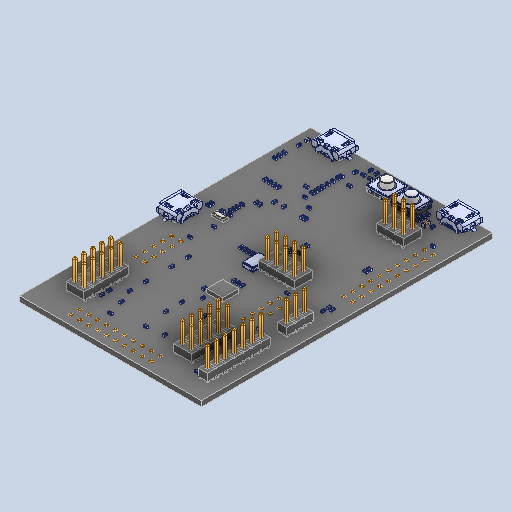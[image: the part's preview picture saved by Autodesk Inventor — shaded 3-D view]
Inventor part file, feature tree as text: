
AUTODESK INVENTOR PART (.ipt)
format: ipt  version: 2024.2 (Build 282272000, 272)  size: 4,771,328 bytes
history: native  units: mm
features: sketch x350, other x149, chamfer x6
ambient origin geometry x8: Origin, YZ Plane, XZ Plane, XY Plane, X Axis, Y Axis, Z Axis, Center Point
bodies: Solid1 (feature_tree), Solid2 (feature_tree), Solid3 (feature_tree), Solid4 (feature_tree), Solid5 (feature_tree), Solid6 (feature_tree), Solid7 (feature_tree), Solid8 (feature_tree), Solid9 (feature_tree), Solid10 (feature_tree), Solid11 (feature_tree), Solid12 (feature_tree), Solid13 (feature_tree), Solid14 (feature_tree), Solid15 (feature_tree), Solid16 (feature_tree), Solid17 (feature_tree), Solid18 (feature_tree), Solid19 (feature_tree), Solid20 (feature_tree), Solid21 (feature_tree), Solid22 (feature_tree), Solid23 (feature_tree), Solid24 (feature_tree), Solid25 (feature_tree), Solid26 (feature_tree), Solid27 (feature_tree), Solid28 (feature_tree), Solid29 (feature_tree), Solid30 (feature_tree), Solid31 (feature_tree), Solid32 (feature_tree), Solid33 (feature_tree), Solid34 (feature_tree), Solid35 (feature_tree), Solid36 (feature_tree), Solid37 (feature_tree), Solid38 (feature_tree), Solid39 (feature_tree), Solid40 (feature_tree), Solid41 (feature_tree), Solid42 (feature_tree), Solid43 (feature_tree), Solid44 (feature_tree), Solid45 (feature_tree), Solid46 (feature_tree), Solid47 (feature_tree), Solid48 (feature_tree), Solid49 (feature_tree), Solid50 (feature_tree), Solid51 (feature_tree), Solid52 (feature_tree), Solid53 (feature_tree), Solid54 (feature_tree), Solid55 (feature_tree), Solid56 (feature_tree), Solid57 (feature_tree), Solid58 (feature_tree), Solid59 (feature_tree), Solid60 (feature_tree), Solid61 (feature_tree), Solid62 (feature_tree), Solid63 (feature_tree), Solid64 (feature_tree), Solid65 (feature_tree), Solid66 (feature_tree), Solid67 (feature_tree), Solid68 (feature_tree), Solid69 (feature_tree), Solid70 (feature_tree), Solid71 (feature_tree), Solid72 (feature_tree), Solid73 (feature_tree), Solid74 (feature_tree), Solid75 (feature_tree), Solid76 (feature_tree), Solid77 (feature_tree), Solid78 (feature_tree), Solid79 (feature_tree), Solid80 (feature_tree), Solid81 (feature_tree), Solid82 (feature_tree), Solid83 (feature_tree), Solid84 (feature_tree), Solid85 (feature_tree), Solid86 (feature_tree), Solid87 (feature_tree), Solid88 (feature_tree), Solid89 (feature_tree), Solid90 (feature_tree), Solid91 (feature_tree), Solid92 (feature_tree), Solid93 (feature_tree), Solid94 (feature_tree), Solid95 (feature_tree), Solid96 (feature_tree), Solid97 (feature_tree), Solid98 (feature_tree), Solid99 (feature_tree), Solid100 (feature_tree), Solid101 (feature_tree), Solid102 (feature_tree), Solid103 (feature_tree), Solid104 (feature_tree), Solid105 (feature_tree), Solid106 (feature_tree), Solid107 (feature_tree), Solid108 (feature_tree), Solid109 (feature_tree), Solid110 (feature_tree), Solid111 (feature_tree), Solid112 (feature_tree), Solid113 (feature_tree), Solid114 (feature_tree), Solid115 (feature_tree), Solid116 (feature_tree), Solid117 (feature_tree), Solid118 (feature_tree), Solid119 (feature_tree), Solid120 (feature_tree), Solid121 (feature_tree), Solid122 (feature_tree), Solid123 (feature_tree), Solid124 (feature_tree), Solid125 (feature_tree), Solid126 (feature_tree), Solid127 (feature_tree), Solid128 (feature_tree), Solid129 (feature_tree), Solid130 (feature_tree), Solid131 (feature_tree), Solid132 (feature_tree), Solid133 (feature_tree), Solid134 (feature_tree), Solid135 (feature_tree), Solid136 (feature_tree), Solid137 (feature_tree), Solid138 (feature_tree), Solid139 (feature_tree), Solid140 (feature_tree), Solid141 (feature_tree), Solid142 (feature_tree), Solid143 (feature_tree), Solid144 (feature_tree), Solid145 (feature_tree), Solid146 (feature_tree), Solid147 (feature_tree), Solid148 (feature_tree), Solid149 (feature_tree), Solid150 (feature_tree), Solid151 (feature_tree), Solid152 (feature_tree), Solid153 (feature_tree), Solid154 (feature_tree), Solid155 (feature_tree), Solid156 (feature_tree), Solid157 (feature_tree), Solid158 (feature_tree), Solid159 (feature_tree), Solid160 (feature_tree), Solid161 (feature_tree), Solid162 (feature_tree), Solid163 (feature_tree), Solid164 (feature_tree), Solid165 (feature_tree), Solid166 (feature_tree), Solid167 (feature_tree), Solid168 (feature_tree), Solid169 (feature_tree), Solid170 (feature_tree), Solid171 (feature_tree), Solid172 (feature_tree), Solid173 (feature_tree), Solid174 (feature_tree), Solid175 (feature_tree), Solid176 (feature_tree), Solid177 (feature_tree), Solid178 (feature_tree), Solid179 (feature_tree), Solid180 (feature_tree), Solid181 (feature_tree), Solid182 (feature_tree), Solid183 (feature_tree), Solid184 (feature_tree), Solid185 (feature_tree), Solid186 (feature_tree), Solid187 (feature_tree), Solid188 (feature_tree), Solid189 (feature_tree), Solid190 (feature_tree), Solid191 (feature_tree), Solid192 (feature_tree), Solid193 (feature_tree), Solid194 (feature_tree), Solid195 (feature_tree), Solid196 (feature_tree), Solid197 (feature_tree), Solid198 (feature_tree), Solid199 (feature_tree), Solid200 (feature_tree), Solid201 (feature_tree), Solid202 (feature_tree), Solid203 (feature_tree), Solid204 (feature_tree), Solid205 (feature_tree), Solid206 (feature_tree), Solid207 (feature_tree), Solid208 (feature_tree), Solid209 (feature_tree), Solid210 (feature_tree), Solid211 (feature_tree), Solid212 (feature_tree), Solid213 (feature_tree), Solid214 (feature_tree), Solid215 (feature_tree), Solid216 (feature_tree), Solid217 (feature_tree), Solid218 (feature_tree), Solid219 (feature_tree), Solid220 (feature_tree), Solid221 (feature_tree), Solid222 (feature_tree), Solid223 (feature_tree), Solid224 (feature_tree), Solid225 (feature_tree), Solid226 (feature_tree), Solid227 (feature_tree), Solid228 (feature_tree), Solid229 (feature_tree), Solid230 (feature_tree), Solid231 (feature_tree), Solid232 (feature_tree), Solid233 (feature_tree), Solid234 (feature_tree), Solid235 (feature_tree), Solid236 (feature_tree), Solid237 (feature_tree), Solid238 (feature_tree), Solid239 (feature_tree), Solid240 (feature_tree), Solid241 (feature_tree), Solid242 (feature_tree), Solid243 (feature_tree), Solid244 (feature_tree), Solid245 (feature_tree), Solid246 (feature_tree), Solid247 (feature_tree), Solid248 (feature_tree), Solid249 (feature_tree), Solid250 (feature_tree), Solid251 (feature_tree), Solid252 (feature_tree), Solid253 (feature_tree), Solid254 (feature_tree), Solid255 (feature_tree), Solid256 (feature_tree), Solid257 (feature_tree), Solid258 (feature_tree), Solid259 (feature_tree), Solid260 (feature_tree), Solid261 (feature_tree), Solid262 (feature_tree), Solid263 (feature_tree), Solid264 (feature_tree), Solid265 (feature_tree), Solid266 (feature_tree), Solid267 (feature_tree), Solid268 (feature_tree), Solid269 (feature_tree), Solid270 (feature_tree), Solid271 (feature_tree), Solid272 (feature_tree), Solid273 (feature_tree), Solid274 (feature_tree), Solid275 (feature_tree), Solid276 (feature_tree), Solid277 (feature_tree), Solid278 (feature_tree), Solid279 (feature_tree), Solid280 (feature_tree), Solid281 (feature_tree), Solid282 (feature_tree), Solid283 (feature_tree), Solid284 (feature_tree), Solid285 (feature_tree), Solid286 (feature_tree), Solid287 (feature_tree), Solid288 (feature_tree), Solid289 (feature_tree), Solid290 (feature_tree), Solid291 (feature_tree), Solid292 (feature_tree), Solid293 (feature_tree), Solid294 (feature_tree), Solid295 (feature_tree), Solid296 (feature_tree), Solid297 (feature_tree), Solid298 (feature_tree), Solid299 (feature_tree), Solid300 (feature_tree), Solid301 (feature_tree), Solid302 (feature_tree), Solid303 (feature_tree), Solid304 (feature_tree), Solid305 (feature_tree), Solid306 (feature_tree), Solid307 (feature_tree), Solid308 (feature_tree), Solid309 (feature_tree), Solid310 (feature_tree), Solid311 (feature_tree), Solid312 (feature_tree), Solid313 (feature_tree), Solid314 (feature_tree), Solid315 (feature_tree), Solid316 (feature_tree), Solid317 (feature_tree), Solid318 (feature_tree), Solid319 (feature_tree), Solid320 (feature_tree), Solid321 (feature_tree), Solid322 (feature_tree), Solid323 (feature_tree), Solid324 (feature_tree), Solid325 (feature_tree), Solid326 (feature_tree), Solid327 (feature_tree), Solid328 (feature_tree), Solid329 (feature_tree), Solid330 (feature_tree), Solid331 (feature_tree), Solid332 (feature_tree), Solid333 (feature_tree), Solid334 (feature_tree), Solid335 (feature_tree), Solid336 (feature_tree), Solid337 (feature_tree), Solid338 (feature_tree), Solid339 (feature_tree), Solid340 (feature_tree), Solid341 (feature_tree), Solid342 (feature_tree), Solid343 (feature_tree), Solid344 (feature_tree), Solid345 (feature_tree), Solid346 (feature_tree), Solid347 (feature_tree), Solid348 (feature_tree), Solid349 (feature_tree), Solid350 (feature_tree), Solid351 (feature_tree), Solid352 (feature_tree), Solid353 (feature_tree), Solid354 (feature_tree), Solid355 (feature_tree), Solid356 (feature_tree), Solid357 (feature_tree), Solid358 (feature_tree), Solid359 (feature_tree), Solid360 (feature_tree), Solid361 (feature_tree), Solid362 (feature_tree), Solid363 (feature_tree), Solid364 (feature_tree), Solid365 (feature_tree), Solid366 (feature_tree), Solid367 (feature_tree), Solid368 (feature_tree), Solid369 (feature_tree), Solid370 (feature_tree), Solid371 (feature_tree), Solid372 (feature_tree), Solid373 (feature_tree), Solid374 (feature_tree), Solid375 (feature_tree), Solid376 (feature_tree), Solid377 (feature_tree), Solid378 (feature_tree), Solid379 (feature_tree), Solid380 (feature_tree), Solid381 (feature_tree), Solid382 (feature_tree), Solid383 (feature_tree), Solid384 (feature_tree), Solid385 (feature_tree), Solid386 (feature_tree), Solid387 (feature_tree), Solid388 (feature_tree), Solid389 (feature_tree), Solid390 (feature_tree), Solid391 (feature_tree), Solid392 (feature_tree), Solid393 (feature_tree), Solid394 (feature_tree), Solid395 (feature_tree), Solid396 (feature_tree), Solid397 (feature_tree), Solid398 (feature_tree), Solid399 (feature_tree), Solid400 (feature_tree), Solid401 (feature_tree), Solid402 (feature_tree), Solid403 (feature_tree), Solid404 (feature_tree), Solid405 (feature_tree), Solid406 (feature_tree), Solid407 (feature_tree), Solid408 (feature_tree), Solid409 (feature_tree), Solid410 (feature_tree), Solid411 (feature_tree), Solid412 (feature_tree), Solid413 (feature_tree), Solid414 (feature_tree), Solid415 (feature_tree), Solid416 (feature_tree), Solid417 (feature_tree), Solid418 (feature_tree), Solid419 (feature_tree), Solid420 (feature_tree), Solid421 (feature_tree), Solid422 (feature_tree), Solid423 (feature_tree), Solid424 (feature_tree), Solid425 (feature_tree), Solid426 (feature_tree), Solid427 (feature_tree), Solid428 (feature_tree), Solid429 (feature_tree), Solid430 (feature_tree), Solid431 (feature_tree), Solid432 (feature_tree), Solid433 (feature_tree), Solid434 (feature_tree), Solid435 (feature_tree), Solid436 (feature_tree), Solid437 (feature_tree), Solid438 (feature_tree), Solid439 (feature_tree), Solid440 (feature_tree), Solid441 (feature_tree), Solid442 (feature_tree), Solid443 (feature_tree), Solid444 (feature_tree), Solid445 (feature_tree), Solid446 (feature_tree), Solid447 (feature_tree), Solid448 (feature_tree), Solid449 (feature_tree), Solid450 (feature_tree), Solid451 (feature_tree), Solid452 (feature_tree), Solid453 (feature_tree), Solid454 (feature_tree), Solid455 (feature_tree), Solid456 (feature_tree), Solid457 (feature_tree), Solid458 (feature_tree), Solid459 (feature_tree), Solid460 (feature_tree), Solid461 (feature_tree), Solid462 (feature_tree), Solid463 (feature_tree), Solid464 (feature_tree), Solid465 (feature_tree), Solid466 (feature_tree), Solid467 (feature_tree), Solid468 (feature_tree), Solid469 (feature_tree), Solid470 (feature_tree), Solid471 (feature_tree), Solid472 (feature_tree), Solid473 (feature_tree), Solid474 (feature_tree), Solid475 (feature_tree), Solid476 (feature_tree), Solid477 (feature_tree), Solid478 (feature_tree), Solid479 (feature_tree), Solid480 (feature_tree), Solid481 (feature_tree), Solid482 (feature_tree), Solid483 (feature_tree), Solid484 (feature_tree), Solid485 (feature_tree), Solid486 (feature_tree), Solid487 (feature_tree), Solid488 (feature_tree), Solid489 (feature_tree), Solid490 (feature_tree), Solid491 (feature_tree), Solid492 (feature_tree), Solid493 (feature_tree), Solid494 (feature_tree), Solid495 (feature_tree), Solid496 (feature_tree), Solid497 (feature_tree), Solid498 (feature_tree), Solid499 (feature_tree), Solid500 (feature_tree), Solid501 (feature_tree), Solid502 (feature_tree), Solid503 (feature_tree), Solid504 (feature_tree), Solid505 (feature_tree)
feature tree (505):
  other  "Boss-Extrude2"
  other  "Split1[1]"
  other  "Split1[2]"
  other  "Split1[3]"
  other  "Boss-Extrude10[1]"
  other  "Boss-Extrude10[2]"
  other  "Boss-Extrude10[3]"
  other  "Boss-Extrude10[4]"
  other  "Boss-Extrude10[5]"
  other  "Boss-Extrude10[6]"
  other  "Boss-Extrude10[7]"
  other  "Boss-Extrude10[8]"
  other  "Boss-Extrude10[9]"
  other  "Boss-Extrude10[10]"
  other  "Boss-Extrude10[11]"
  other  "Boss-Extrude10[12]"
  other  "Boss-Extrude10[13]"
  other  "Boss-Extrude10[14]"
  other  "Boss-Extrude10[15]"
  other  "Boss-Extrude10[16]"
  other  "Boss-Extrude10[17]"
  other  "Boss-Extrude10[18]"
  other  "Boss-Extrude10[19]"
  other  "Boss-Extrude10[20]"
  other  "Boss-Extrude10[21]"
  other  "Boss-Extrude10[22]"
  other  "Boss-Extrude10[23]"
  other  "Boss-Extrude10[24]"
  other  "Boss-Extrude10[25]"
  other  "Boss-Extrude10[26]"
  other  "Boss-Extrude10[27]"
  other  "Boss-Extrude10[28]"
  other  "Boss-Extrude10[29]"
  other  "Boss-Extrude10[30]"
  other  "Boss-Extrude10[31]"
  other  "Boss-Extrude10[32]"
  other  "Boss-Extrude10[33]"
  other  "Boss-Extrude10[34]"
  other  "Boss-Extrude10[35]"
  other  "Boss-Extrude10[36]"
  other  "Boss-Extrude10[37]"
  other  "Boss-Extrude10[38]"
  other  "Boss-Extrude10[39]"
  other  "Boss-Extrude10[40]"
  other  "Boss-Extrude10[41]"
  other  "Boss-Extrude10[42]"
  other  "Boss-Extrude10[43]"
  other  "Boss-Extrude10[44]"
  other  "Boss-Extrude10[45]"
  other  "Boss-Extrude10[46]"
  other  "Boss-Extrude10[47]"
  other  "Boss-Extrude10[48]"
  other  "Boss-Extrude10[49]"
  other  "Boss-Extrude10[50]"
  other  "Boss-Extrude10[51]"
  other  "Boss-Extrude10[52]"
  other  "Boss-Extrude10[53]"
  other  "Boss-Extrude10[54]"
  other  "Boss-Extrude10[55]"
  other  "Boss-Extrude10[56]"
  other  "Boss-Extrude10[57]"
  other  "Boss-Extrude10[58]"
  other  "Boss-Extrude10[59]"
  other  "Boss-Extrude10[60]"
  other  "LPattern2[1]"
  other  "LPattern2[2]"
  other  "LPattern2[3]"
  other  "LPattern2[4]"
  other  "LPattern2[5]"
  other  "LPattern3[1]"
  other  "LPattern3[2]"
  other  "LPattern3[3]"
  other  "LPattern3[4]"
  other  "LPattern3[5]"
  other  "LPattern3[6]"
  other  "LPattern3[7]"
  other  "LPattern4[1]"
  other  "LPattern4[2]"
  other  "LPattern4[3]"
  other  "LPattern4[4]"
  other  "LPattern4[5]"
  other  "LPattern4[6]"
  other  "LPattern4[7]"
  other  "LPattern4[8]"
  other  "LPattern4[9]"
  other  "LPattern4[10]"
  other  "LPattern4[11]"
  other  "LPattern4[12]"
  other  "LPattern4[13]"
  other  "LPattern4[14]"
  other  "LPattern4[15]"
  other  "LPattern4[16]"
  other  "LPattern4[17]"
  other  "LPattern4[18]"
  other  "LPattern5[1]"
  other  "LPattern5[2]"
  other  "LPattern6[1]"
  other  "LPattern6[2]"
  other  "LPattern6[3]"
  other  "LPattern6[4]"
  other  "LPattern6[5]"
  other  "LPattern6[6]"
  sketch  "Sketch-Pattern1[2]"
  sketch  "Sketch-Pattern1[5]"
  sketch  "Sketch-Pattern1[8]"
  sketch  "Sketch-Pattern1[11]"
  sketch  "Sketch-Pattern1[14]"
  sketch  "Sketch-Pattern1[17]"
  sketch  "Sketch-Pattern1[20]"
  other  "Body-Move_Copy3[1]"
  other  "Body-Move_Copy3[2]"
  other  "Body-Move_Copy3[3]"
  other  "Body-Move_Copy3[4]"
  other  "Body-Move_Copy3[5]"
  other  "Body-Move_Copy3[6]"
  other  "Body-Move_Copy3[7]"
  other  "Body-Move_Copy4[1]"
  other  "Body-Move_Copy4[2]"
  other  "Body-Move_Copy4[3]"
  other  "Body-Move_Copy4[4]"
  other  "Body-Move_Copy4[5]"
  other  "Body-Move_Copy4[6]"
  other  "Body-Move_Copy4[7]"
  other  "Cut-Extrude6[1]"
  chamfer  "Chamfer8"  [1 undecoded]
  chamfer  "Chamfer9"  [1 undecoded]
  chamfer  "Chamfer10"  [1 undecoded]
  chamfer  "Chamfer7"  [1 undecoded]
  chamfer  "Chamfer6"  [1 undecoded]
  chamfer  "Chamfer5"  [1 undecoded]
  other  "Cut-Extrude8"
  other  "_skraake010_-_Boss-Extrude1_"
  other  "_skraake010_-_Cut-Extrude2[1]_"
  other  "_skraake010_-_Boss-Extrude2_"
  other  "LPattern7[1]"
  other  "LPattern7[2]"
  other  "LPattern7[3]"
  other  "Boss-Extrude15[1]"
  other  "Boss-Extrude15[2]"
  other  "Boss-Extrude16"
  sketch  "Sketch-Pattern2[1]"
  sketch  "Sketch-Pattern2[2]"
  sketch  "Sketch-Pattern2[3]"
  sketch  "Sketch-Pattern2[4]"
  sketch  "Sketch-Pattern2[5]"
  sketch  "Sketch-Pattern2[6]"
  sketch  "Sketch-Pattern2[8]"
  sketch  "Sketch-Pattern2[9]"
  sketch  "Sketch-Pattern2[10]"
  sketch  "Sketch-Pattern2[11]"
  sketch  "Sketch-Pattern2[12]"
  sketch  "Sketch-Pattern2[13]"
  sketch  "Sketch-Pattern2[14]"
  sketch  "Sketch-Pattern2[15]"
  sketch  "Sketch-Pattern2[16]"
  sketch  "Sketch-Pattern2[17]"
  sketch  "Sketch-Pattern2[18]"
  sketch  "Sketch-Pattern2[19]"
  sketch  "Sketch-Pattern2[20]"
  sketch  "Sketch-Pattern2[21]"
  sketch  "Sketch-Pattern2[22]"
  sketch  "Sketch-Pattern2[23]"
  sketch  "Sketch-Pattern2[24]"
  sketch  "Sketch-Pattern2[25]"
  sketch  "Sketch-Pattern2[26]"
  sketch  "Sketch-Pattern2[27]"
  sketch  "Sketch-Pattern2[28]"
  sketch  "Sketch-Pattern2[29]"
  sketch  "Sketch-Pattern2[30]"
  sketch  "Sketch-Pattern2[31]"
  sketch  "Sketch-Pattern2[32]"
  sketch  "Sketch-Pattern2[33]"
  sketch  "Sketch-Pattern2[34]"
  sketch  "Sketch-Pattern2[35]"
  sketch  "Sketch-Pattern2[36]"
  sketch  "Sketch-Pattern2[37]"
  sketch  "Sketch-Pattern2[38]"
  sketch  "Sketch-Pattern2[39]"
  sketch  "Sketch-Pattern2[41]"
  sketch  "Sketch-Pattern2[42]"
  sketch  "Sketch-Pattern2[43]"
  sketch  "Sketch-Pattern2[44]"
  sketch  "Sketch-Pattern2[45]"
  sketch  "Sketch-Pattern2[46]"
  sketch  "Sketch-Pattern2[47]"
  sketch  "Sketch-Pattern2[48]"
  sketch  "Sketch-Pattern2[49]"
  sketch  "Sketch-Pattern2[50]"
  sketch  "Sketch-Pattern2[51]"
  sketch  "Sketch-Pattern2[52]"
  sketch  "Sketch-Pattern2[53]"
  sketch  "Sketch-Pattern2[54]"
  sketch  "Sketch-Pattern2[55]"
  sketch  "Sketch-Pattern2[56]"
  sketch  "Sketch-Pattern2[57]"
  sketch  "Sketch-Pattern2[58]"
  sketch  "Sketch-Pattern2[59]"
  sketch  "Sketch-Pattern2[60]"
  sketch  "Sketch-Pattern2[61]"
  sketch  "Sketch-Pattern2[62]"
  sketch  "Sketch-Pattern2[63]"
  sketch  "Sketch-Pattern2[64]"
  sketch  "Sketch-Pattern2[65]"
  sketch  "Sketch-Pattern2[66]"
  sketch  "Sketch-Pattern2[67]"
  sketch  "Sketch-Pattern2[68]"
  sketch  "Sketch-Pattern2[69]"
  sketch  "Sketch-Pattern2[70]"
  sketch  "Sketch-Pattern2[71]"
  sketch  "Sketch-Pattern2[72]"
  sketch  "Sketch-Pattern2[74]"
  sketch  "Sketch-Pattern2[75]"
  sketch  "Sketch-Pattern2[76]"
  sketch  "Sketch-Pattern2[77]"
  sketch  "Sketch-Pattern2[78]"
  sketch  "Sketch-Pattern2[79]"
  sketch  "Sketch-Pattern2[80]"
  sketch  "Sketch-Pattern2[81]"
  sketch  "Sketch-Pattern2[82]"
  sketch  "Sketch-Pattern2[83]"
  sketch  "Sketch-Pattern2[84]"
  sketch  "Sketch-Pattern2[85]"
  sketch  "Sketch-Pattern2[86]"
  sketch  "Sketch-Pattern2[87]"
  sketch  "Sketch-Pattern2[88]"
  sketch  "Sketch-Pattern2[89]"
  sketch  "Sketch-Pattern2[90]"
  sketch  "Sketch-Pattern2[91]"
  sketch  "Sketch-Pattern2[92]"
  sketch  "Sketch-Pattern2[93]"
  sketch  "Sketch-Pattern2[94]"
  sketch  "Sketch-Pattern2[95]"
  sketch  "Sketch-Pattern2[96]"
  sketch  "Sketch-Pattern2[97]"
  sketch  "Sketch-Pattern2[98]"
  sketch  "Sketch-Pattern2[99]"
  sketch  "Sketch-Pattern2[100]"
  sketch  "Sketch-Pattern2[101]"
  sketch  "Sketch-Pattern2[102]"
  sketch  "Sketch-Pattern2[103]"
  sketch  "Sketch-Pattern2[104]"
  sketch  "Sketch-Pattern2[105]"
  sketch  "Sketch-Pattern2[106]"
  sketch  "Sketch-Pattern2[107]"
  sketch  "Sketch-Pattern2[108]"
  other  "Body-Move_Copy7[1]"
  other  "Body-Move_Copy7[2]"
  other  "Body-Move_Copy7[3]"
  sketch  "Sketch-Pattern2[109]"
  sketch  "Sketch-Pattern2[110]"
  sketch  "Sketch-Pattern2[111]"
  sketch  "Sketch-Pattern2[112]"
  sketch  "Sketch-Pattern2[113]"
  sketch  "Sketch-Pattern2[114]"
  sketch  "Sketch-Pattern3[1]"
  sketch  "Sketch-Pattern3[2]"
  sketch  "Sketch-Pattern3[3]"
  sketch  "Sketch-Pattern3[4]"
  sketch  "Sketch-Pattern3[5]"
  sketch  "Sketch-Pattern3[6]"
  sketch  "Sketch-Pattern3[7]"
  sketch  "Sketch-Pattern3[8]"
  sketch  "Sketch-Pattern3[9]"
  sketch  "Sketch-Pattern3[10]"
  sketch  "Sketch-Pattern3[11]"
  sketch  "Sketch-Pattern3[12]"
  sketch  "Sketch-Pattern3[13]"
  sketch  "Sketch-Pattern3[14]"
  sketch  "Sketch-Pattern3[15]"
  sketch  "Sketch-Pattern3[16]"
  sketch  "Sketch-Pattern3[17]"
  sketch  "Sketch-Pattern3[18]"
  sketch  "Sketch-Pattern3[19]"
  sketch  "Sketch-Pattern3[20]"
  sketch  "Sketch-Pattern3[21]"
  sketch  "Sketch-Pattern3[22]"
  sketch  "Sketch-Pattern3[23]"
  sketch  "Sketch-Pattern3[24]"
  sketch  "Sketch-Pattern3[25]"
  sketch  "Sketch-Pattern3[26]"
  sketch  "Sketch-Pattern3[27]"
  sketch  "Sketch-Pattern3[28]"
  sketch  "Sketch-Pattern3[29]"
  sketch  "Sketch-Pattern3[30]"
  sketch  "Sketch-Pattern3[31]"
  sketch  "Sketch-Pattern3[32]"
  sketch  "Sketch-Pattern3[33]"
  sketch  "Sketch-Pattern3[34]"
  sketch  "Sketch-Pattern3[35]"
  sketch  "Sketch-Pattern3[36]"
  sketch  "Sketch-Pattern3[37]"
  sketch  "Sketch-Pattern3[38]"
  sketch  "Sketch-Pattern3[39]"
  sketch  "Sketch-Pattern3[40]"
  sketch  "Sketch-Pattern3[41]"
  sketch  "Sketch-Pattern3[42]"
  sketch  "Sketch-Pattern3[43]"
  sketch  "Sketch-Pattern3[44]"
  sketch  "Sketch-Pattern3[45]"
  sketch  "Sketch-Pattern3[46]"
  sketch  "Sketch-Pattern3[47]"
  sketch  "Sketch-Pattern3[48]"
  sketch  "Sketch-Pattern3[49]"
  sketch  "Sketch-Pattern3[50]"
  sketch  "Sketch-Pattern3[51]"
  sketch  "Sketch-Pattern3[52]"
  sketch  "Sketch-Pattern3[53]"
  sketch  "Sketch-Pattern3[54]"
  sketch  "Sketch-Pattern3[55]"
  sketch  "Sketch-Pattern3[56]"
  sketch  "Sketch-Pattern3[57]"
  sketch  "Sketch-Pattern3[58]"
  sketch  "Sketch-Pattern3[59]"
  sketch  "Sketch-Pattern3[60]"
  sketch  "Sketch-Pattern3[61]"
  sketch  "Sketch-Pattern3[62]"
  sketch  "Sketch-Pattern3[63]"
  sketch  "Sketch-Pattern3[64]"
  sketch  "Sketch-Pattern3[65]"
  sketch  "Sketch-Pattern3[66]"
  sketch  "Sketch-Pattern3[67]"
  sketch  "Sketch-Pattern3[68]"
  sketch  "Sketch-Pattern3[69]"
  sketch  "Sketch-Pattern3[70]"
  sketch  "Sketch-Pattern3[71]"
  sketch  "Sketch-Pattern3[72]"
  sketch  "Sketch-Pattern3[73]"
  sketch  "Sketch-Pattern3[74]"
  sketch  "Sketch-Pattern3[75]"
  sketch  "Sketch-Pattern3[76]"
  sketch  "Sketch-Pattern3[77]"
  sketch  "Sketch-Pattern3[78]"
  sketch  "Sketch-Pattern3[79]"
  sketch  "Sketch-Pattern3[80]"
  sketch  "Sketch-Pattern3[81]"
  sketch  "Sketch-Pattern3[82]"
  sketch  "Sketch-Pattern3[83]"
  sketch  "Sketch-Pattern3[84]"
  sketch  "Sketch-Pattern3[85]"
  sketch  "Sketch-Pattern3[86]"
  sketch  "Sketch-Pattern3[87]"
  sketch  "Sketch-Pattern3[88]"
  sketch  "Sketch-Pattern3[89]"
  sketch  "Sketch-Pattern3[90]"
  sketch  "Sketch-Pattern3[91]"
  sketch  "Sketch-Pattern3[92]"
  sketch  "Sketch-Pattern3[93]"
  sketch  "Sketch-Pattern3[94]"
  sketch  "Sketch-Pattern3[95]"
  sketch  "Sketch-Pattern3[96]"
  sketch  "Sketch-Pattern3[97]"
  sketch  "Sketch-Pattern3[98]"
  sketch  "Sketch-Pattern3[99]"
  sketch  "Sketch-Pattern3[100]"
  sketch  "Sketch-Pattern3[101]"
  sketch  "Sketch-Pattern3[102]"
  sketch  "Sketch-Pattern3[103]"
  sketch  "Sketch-Pattern3[104]"
  sketch  "Sketch-Pattern3[105]"
  sketch  "Sketch-Pattern3[106]"
  sketch  "Sketch-Pattern3[107]"
  sketch  "Sketch-Pattern3[108]"
  sketch  "Sketch-Pattern3[109]"
  sketch  "Sketch-Pattern3[110]"
  sketch  "Sketch-Pattern3[111]"
  sketch  "Sketch-Pattern3[112]"
  sketch  "Sketch-Pattern3[113]"
  sketch  "Sketch-Pattern3[114]"
  sketch  "Sketch-Pattern3[115]"
  sketch  "Sketch-Pattern3[116]"
  sketch  "Sketch-Pattern3[117]"
  sketch  "Sketch-Pattern3[118]"
  sketch  "Sketch-Pattern3[119]"
  sketch  "Sketch-Pattern3[120]"
  sketch  "Sketch-Pattern3[121]"
  sketch  "Sketch-Pattern3[122]"
  sketch  "Sketch-Pattern3[123]"
  sketch  "Sketch-Pattern3[124]"
  sketch  "Sketch-Pattern3[125]"
  sketch  "Sketch-Pattern3[126]"
  sketch  "Sketch-Pattern2[115]"
  sketch  "Sketch-Pattern2[116]"
  sketch  "Sketch-Pattern2[117]"
  sketch  "Sketch-Pattern2[118]"
  sketch  "Sketch-Pattern2[119]"
  sketch  "Sketch-Pattern2[120]"
  sketch  "Sketch-Pattern2[121]"
  sketch  "Sketch-Pattern2[122]"
  sketch  "Sketch-Pattern2[123]"
  sketch  "Sketch-Pattern3[127]"
  sketch  "Sketch-Pattern3[128]"
  sketch  "Sketch-Pattern3[129]"
  sketch  "Sketch-Pattern3[130]"
  sketch  "Sketch-Pattern3[131]"
  sketch  "Sketch-Pattern3[132]"
  sketch  "Sketch-Pattern3[133]"
  sketch  "Sketch-Pattern3[134]"
  sketch  "Sketch-Pattern3[135]"
  sketch  "Sketch-Pattern3[136]"
  sketch  "Sketch-Pattern3[137]"
  sketch  "Sketch-Pattern3[138]"
  sketch  "Sketch-Pattern4[1]"
  sketch  "Sketch-Pattern4[2]"
  sketch  "Sketch-Pattern4[3]"
  sketch  "Sketch-Pattern4[4]"
  sketch  "Sketch-Pattern4[5]"
  sketch  "Sketch-Pattern4[6]"
  sketch  "Sketch-Pattern4[7]"
  sketch  "Sketch-Pattern4[8]"
  sketch  "Sketch-Pattern4[9]"
  sketch  "Sketch-Pattern4[10]"
  sketch  "Sketch-Pattern4[11]"
  sketch  "Sketch-Pattern4[12]"
  sketch  "Sketch-Pattern4[13]"
  sketch  "Sketch-Pattern4[14]"
  sketch  "Sketch-Pattern4[15]"
  sketch  "Sketch-Pattern4[16]"
  sketch  "Sketch-Pattern4[17]"
  sketch  "Sketch-Pattern4[18]"
  sketch  "Sketch-Pattern4[19]"
  sketch  "Sketch-Pattern4[20]"
  sketch  "Sketch-Pattern4[21]"
  sketch  "Sketch-Pattern4[22]"
  sketch  "Sketch-Pattern4[23]"
  sketch  "Sketch-Pattern4[24]"
  sketch  "Sketch-Pattern4[25]"
  sketch  "Sketch-Pattern4[26]"
  sketch  "Sketch-Pattern4[27]"
  sketch  "Sketch-Pattern4[28]"
  sketch  "Sketch-Pattern4[29]"
  sketch  "Sketch-Pattern4[30]"
  sketch  "Sketch-Pattern4[31]"
  sketch  "Sketch-Pattern4[32]"
  sketch  "Sketch-Pattern4[33]"
  sketch  "Sketch-Pattern4[34]"
  sketch  "Sketch-Pattern4[35]"
  sketch  "Sketch-Pattern4[36]"
  sketch  "Sketch-Pattern4[37]"
  sketch  "Sketch-Pattern4[38]"
  sketch  "Sketch-Pattern4[39]"
  sketch  "Sketch-Pattern4[40]"
  sketch  "Sketch-Pattern4[41]"
  sketch  "Sketch-Pattern4[42]"
  sketch  "Sketch-Pattern4[43]"
  sketch  "Sketch-Pattern4[44]"
  sketch  "Sketch-Pattern4[45]"
  sketch  "Sketch-Pattern4[46]"
  sketch  "Sketch-Pattern4[47]"
  sketch  "Sketch-Pattern4[48]"
  sketch  "Sketch-Pattern4[49]"
  sketch  "Sketch-Pattern4[50]"
  sketch  "Sketch-Pattern4[51]"
  sketch  "Sketch-Pattern5[1]"
  sketch  "Sketch-Pattern5[2]"
  sketch  "Sketch-Pattern5[3]"
  sketch  "Sketch-Pattern5[4]"
  sketch  "Sketch-Pattern5[5]"
  sketch  "Sketch-Pattern5[6]"
  sketch  "Sketch-Pattern5[7]"
  sketch  "Sketch-Pattern5[8]"
  sketch  "Sketch-Pattern5[9]"
  sketch  "Sketch-Pattern5[10]"
  sketch  "Sketch-Pattern5[11]"
  sketch  "Sketch-Pattern5[12]"
  sketch  "Sketch-Pattern5[13]"
  sketch  "Sketch-Pattern5[14]"
  sketch  "Sketch-Pattern5[15]"
  sketch  "Sketch-Pattern5[16]"
  sketch  "Sketch-Pattern5[17]"
  sketch  "Sketch-Pattern5[18]"
  sketch  "Sketch-Pattern5[19]"
  sketch  "Sketch-Pattern5[20]"
  sketch  "Sketch-Pattern5[21]"
  sketch  "Sketch-Pattern5[22]"
  sketch  "Sketch-Pattern5[23]"
  sketch  "Sketch-Pattern5[24]"
  sketch  "Sketch-Pattern5[25]"
  sketch  "Sketch-Pattern5[26]"
  sketch  "Sketch-Pattern5[27]"
  sketch  "Sketch-Pattern5[28]"
  sketch  "Sketch-Pattern5[29]"
  sketch  "Sketch-Pattern5[30]"
  parser-record x1  (decoder bookkeeping rows leaked as tree rows — omitted from the tree; the rows remain in map.json)
  other  "_GRM188R61A106KE69D_-_Boss-Extrude2_"
  other  "_GRM188R61A106KE69D_-_Mirror2_"
  sketch  "Sketch-Pattern6[1]"
  sketch  "Sketch-Pattern6[2]"
  other  "NONE:1"
  sketch  "Sketch-Pattern7[1]"
  sketch  "Sketch-Pattern7[2]"
  other  "NONE:2"
  other  "Boss-Extrude17"
  other  "Boss-Extrude18"
  other  "NONE:3"
  other  "_ABM3B-13.560MHZ-B-4-Y-T_-_Body-Move_Copy1[5]_"
  other  "_ABM3B-13.560MHZ-B-4-Y-T_-_Body-Move_Copy1[3]_"
  other  "_ABM3B-13.560MHZ-B-4-Y-T_-_Body-Move_Copy1[7]_"
  other  "_ABM3B-13.560MHZ-B-4-Y-T_-_Body-Move_Copy1[1]_"
  other  "_ABM3B-13.560MHZ-B-4-Y-T_-_Body-Move_Copy1[4]_"
  other  "_ABM3B-13.560MHZ-B-4-Y-T_-_Body-Move_Copy1[6]_"
  other  "Cut-Extrude9"
  other  "Cut-Extrude10[1]"
  other  "Cut-Extrude10[2]"
  other  "Cut-Extrude11[1]"
  other  "Cut-Extrude11[2]"
note: 6 required parameter values undecoded (feature->parameter linkage not recoverable at this tier; creation-order binding heuristic only, values carry confidence <= 0.55)
